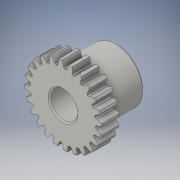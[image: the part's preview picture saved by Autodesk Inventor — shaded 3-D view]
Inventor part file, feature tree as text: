
AUTODESK INVENTOR PART (.ipt)
format: ipt  version: 2016 (Build 200138000, 138)  size: 641,536 bytes
history: native  units: in
note: dims shown in document units (in); Inventor stores cm internally (conversion verified against a paired STEP export)
features: chamfer x1
ambient origin geometry x8: Origin, YZ Plane, XZ Plane, XY Plane, X Axis, Y Axis, Z Axis, Center Point
bodies: Solid1 (feature_tree)
feature tree (1):
  chamfer  "Chamfer1"  [1 undecoded]
note: 1 required parameter value undecoded (feature->parameter linkage not recoverable at this tier; creation-order binding heuristic only, values carry confidence <= 0.55)
